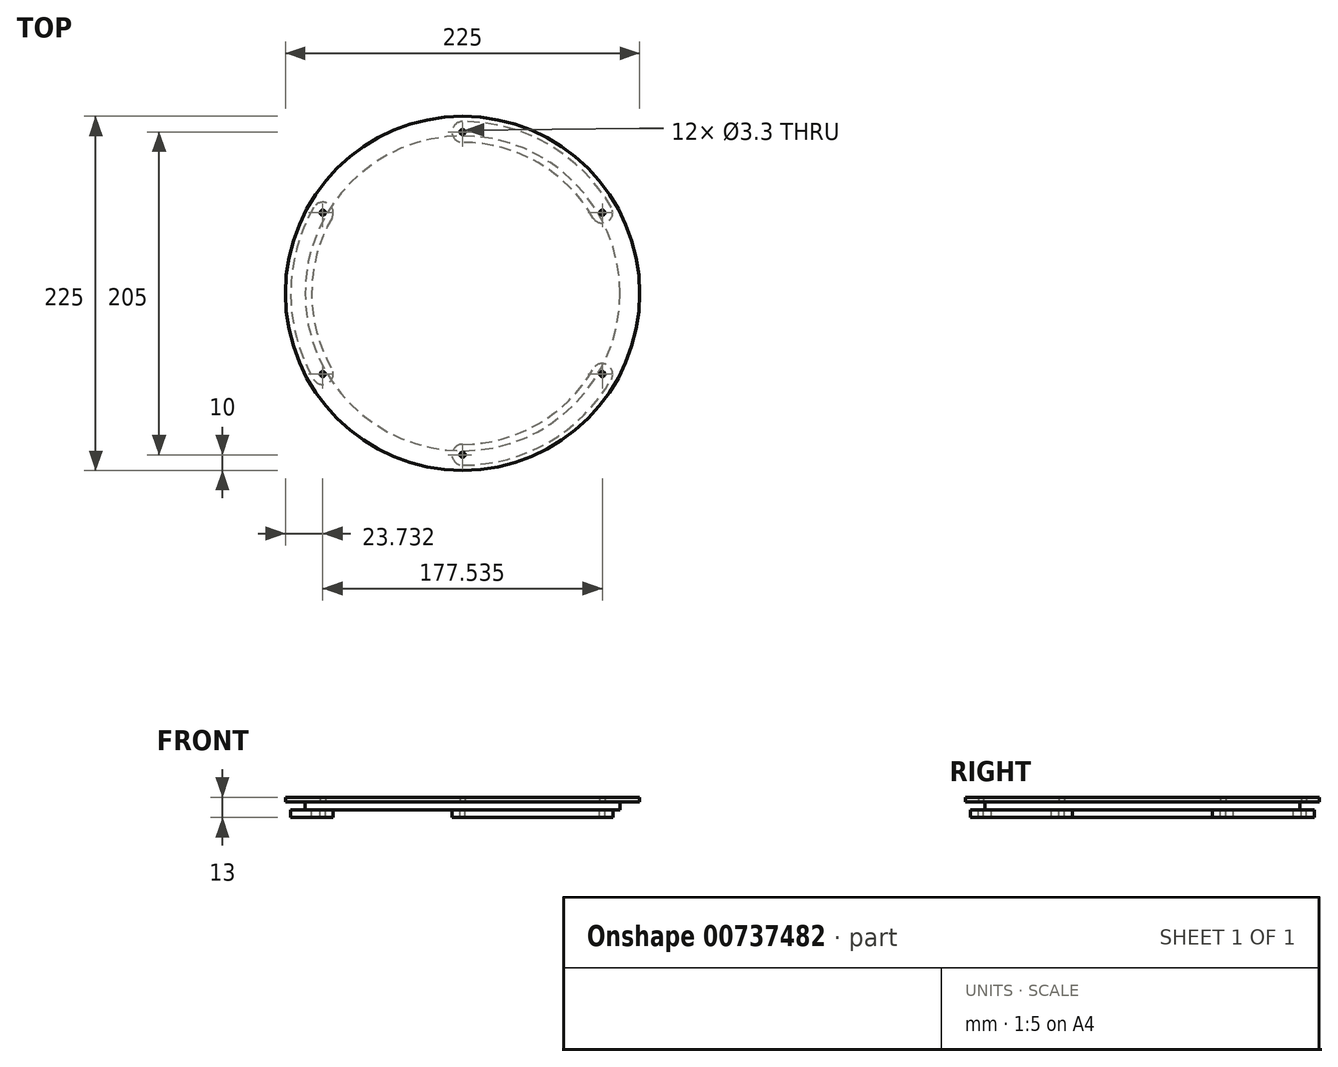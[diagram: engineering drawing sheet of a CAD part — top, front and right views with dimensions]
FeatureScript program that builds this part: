
annotation { "Feature Type Name" : "Feature", "Feature Type Description" : "" }
export const myFeature = defineFeature(function(context is Context, id is Id, definition is map)
    precondition{}
    {
        {
            var Q0;
            Q0=qCreatedBy(makeId("Top.planeOp"),FACE);
            var sketch = newSketch(context, id + "F0", { "sketchPlane" : qUnion([Q0])});
            skCircle(sketch, "E0", {"center": v(0, 0) * mm, "radius": 112.5 * mm});
            skPoint(sketch, "E1", {"position": v(0, 102.5) * mm});
            skPoint(sketch, "E2.1.0", {"position": v(-88.77, 51.25) * mm});
            skPoint(sketch, "E2.2.0", {"position": v(-88.77, -51.25) * mm});
            skPoint(sketch, "E2.3.0", {"position": v(0, -102.5) * mm});
            skPoint(sketch, "E2.4.0", {"position": v(88.77, -51.25) * mm});
            skPoint(sketch, "E2.5.0", {"position": v(88.77, 51.25) * mm});
            skSolve(sketch);
        }
        {
            var Q0;
            Q0=makeQuery(id+"F0.imprint","IMPRINT",FACE,{"disambiguationData":[TD([[makeQuery(id+"F0.imprint","IMPRINT",EDGE,{"derivedFrom":sQuery(id+"F0.wireOp",EDGE,"E0")}),1.0]])]});
            extrude(context, id + "F1", {"entities" : qUnion([Q0]), "depth" : 3 * mm, "offsetDistance" : 25 * mm});
        }
        {
            var Q0;
            Q0=sQuery(id+"F0.wireOp",VERTEX,"E1");
            var Q1;
            Q1=sQuery(id+"F0.wireOp",VERTEX,"E2.1.0");
            var Q2;
            Q2=sQuery(id+"F0.wireOp",VERTEX,"E2.2.0");
            var Q3;
            Q3=sQuery(id+"F0.wireOp",VERTEX,"E2.3.0");
            var Q4;
            Q4=sQuery(id+"F0.wireOp",VERTEX,"E2.4.0");
            var Q5;
            Q5=sQuery(id+"F0.wireOp",VERTEX,"E2.5.0");
            var Q6;
            Q6=makeQuery(id+"F1.opExtrude","SWEPT_BODY",BODY,{"disambiguationData":[OSD([sQuery(id+"F0.wireOp",EDGE,"E0")])]});
            hole(context, id + "F2", {"style" : HoleStyle.SIMPLE, "endStyle" : HoleEndStyle.BLIND, "oppositeDirection" : true, "standardTappedOrClearance" : lookupTablePath({ "standard" : "ISO", "fit" : "Normal", "size" : "M3", "type" : "Clearance" }), "standardBlindInLast" : lookupTablePath({ "fit" : "Standard", "standard" : "ISO", "size" : "M3", "type" : "Clearance" }), "holeDiameter" : 3.3 * mm, "majorDiameter" : 5 * mm, "holeDepth" : 15 * mm, "isTappedThrough" : true, "tappedDepth" : 8.5 * mm, "tapClearance" : 3, "startFromSketch" : true, "locations" : qUnion([Q0, Q1, Q2, Q3, Q4, Q5]), "scope" : qUnion([Q6])});
        }
        {
            var Q0;
            Q0=makeQuery(id+"F0.imprint","IMPRINT",FACE,{"disambiguationData":[TD([[makeQuery(id+"F0.imprint","IMPRINT",EDGE,{"derivedFrom":sQuery(id+"F0.wireOp",EDGE,"E0")}),1.0]])]});
            var sketch = newSketch(context, id + "F3", { "sketchPlane" : qUnion([Q0])});
            skCircle(sketch, "E3", {"center": v(0, 0) * mm, "radius": 100 * mm});
            skSolve(sketch);
        }
        {
            var Q0;
            Q0=makeQuery(id+"F3.imprint","IMPRINT",FACE,{"disambiguationData":[TD([[makeQuery(id+"F3.imprint","IMPRINT",EDGE,{"derivedFrom":sQuery(id+"F3.wireOp",EDGE,"E3")}),1.0]])]});
            extrude(context, id + "F4", {"entities" : qUnion([Q0]), "oppositeDirection" : true, "depth" : 5 * mm, "offsetDistance" : 25 * mm});
        }
        {
            var Q0;
            Q0=makeQuery(id+"F4.opExtrude","CAP_FACE",FACE,{"disambiguationData":[OSD([sQuery(id+"F3.wireOp",EDGE,"E3")])],"isStart":false});
            var sketch = newSketch(context, id + "F5", { "sketchPlane" : qUnion([Q0])});
            skCircle(sketch, "E4", {"center": v(0, -102.5) * mm, "radius": 6.65 * mm});
            skCircle(sketch, "E5", {"center": v(88.77, -51.25) * mm, "radius": 6.65 * mm});
            skArc(sketch, "E6", {"start": v(0, -109.15) * mm, "mid": v(54.57, -94.53) * mm, "end": v(94.53, -54.58) * mm});
            skArc(sketch, "E7", {"start": v(0, -95.85) * mm, "mid": v(47.92, -83) * mm, "end": v(83, -47.93) * mm});
            skCircle(sketch, "E8.0", {"center": v(0, -102.5) * mm, "radius": 1.65 * mm});
            skCircle(sketch, "E8.1", {"center": v(88.77, -51.25) * mm, "radius": 1.65 * mm});
            skSolve(sketch);
        }
        {
            var Q0;
            {var subQ0=sQuery(id+"F5.wireOp",EDGE,"E4");var subQ1=makeQuery(id+"F5.imprint","INTERSECT",VERTEX,{"derivedFrom":[subQ0,sQuery(id+"F5.wireOp",EDGE,"E7")]});Q0=makeQuery(id+"F5.imprint","IMPRINT",FACE,{"disambiguationData":[TD([[makeQuery(id+"F5.imprint","IMPRINT",EDGE,{"disambiguationData":[TD([[subQ1,1.0]])],"derivedFrom":subQ0}),1.0]])]});}
            var Q1;
            {var subQ0=sQuery(id+"F5.wireOp",EDGE,"E4");var subQ1=makeQuery(id+"F5.imprint","INTERSECT",VERTEX,{"derivedFrom":[subQ0,sQuery(id+"F5.wireOp",EDGE,"E6")]});Q1=makeQuery(id+"F5.imprint","IMPRINT",FACE,{"disambiguationData":[TD([[makeQuery(id+"F5.imprint","IMPRINT",EDGE,{"disambiguationData":[TD([[subQ1,1.0]])],"derivedFrom":subQ0}),1.0]])]});}
            var Q2;
            {var subQ0=sQuery(id+"F5.wireOp",EDGE,"E7");Q2=makeQuery(id+"F5.imprint","IMPRINT",FACE,{"disambiguationData":[TD([[makeQuery(id+"F5.imprint","IMPRINT",EDGE,{"derivedFrom":subQ0}),-1.0]])]});}
            var Q3;
            {var subQ0=sQuery(id+"F5.wireOp",EDGE,"E6");Q3=makeQuery(id+"F5.imprint","IMPRINT",FACE,{"disambiguationData":[TD([[makeQuery(id+"F5.imprint","IMPRINT",EDGE,{"derivedFrom":subQ0}),1.0]])]});}
            var Q4;
            {var subQ0=sQuery(id+"F5.wireOp",EDGE,"E5");var subQ1=makeQuery(id+"F5.imprint","INTERSECT",VERTEX,{"derivedFrom":[subQ0,sQuery(id+"F5.wireOp",EDGE,"E7")]});Q4=makeQuery(id+"F5.imprint","IMPRINT",FACE,{"disambiguationData":[TD([[makeQuery(id+"F5.imprint","IMPRINT",EDGE,{"disambiguationData":[TD([[subQ1,1.0]])],"derivedFrom":subQ0}),1.0]])]});}
            var Q5;
            {var subQ0=sQuery(id+"F5.wireOp",EDGE,"E5");var subQ1=makeQuery(id+"F5.imprint","INTERSECT",VERTEX,{"derivedFrom":[subQ0,sQuery(id+"F5.wireOp",EDGE,"E6")]});Q5=makeQuery(id+"F5.imprint","IMPRINT",FACE,{"disambiguationData":[TD([[makeQuery(id+"F5.imprint","IMPRINT",EDGE,{"disambiguationData":[TD([[subQ1,1.0]])],"derivedFrom":subQ0}),1.0]])]});}
            extrude(context, id + "F6", {"entities" : qUnion([Q0, Q1, Q2, Q3, Q4, Q5]), "depth" : 5 * mm, "offsetDistance" : 25 * mm});
        }
        {
            var Q0;
            Q0=qCreatedBy(makeId("Front.planeOp"),FACE);
            var sketch = newSketch(context, id + "F7", { "sketchPlane" : qUnion([Q0])});
            skLineSegment(sketch, "E9", {"start": v(0, 0) * mm, "end": v(0, -38.9) * mm, "construction": true});
            skSolve(sketch);
        }
        {
            var Q0;
            Q0=makeQuery(id+"F6.opExtrude","SWEPT_BODY",BODY,{"disambiguationData":[OSD([sQuery(id+"F5.wireOp",EDGE,"E4"),sQuery(id+"F5.wireOp",EDGE,"E5"),sQuery(id+"F5.wireOp",EDGE,"E6"),sQuery(id+"F5.wireOp",EDGE,"E7"),sQuery(id+"F5.wireOp",EDGE,"E8.0"),sQuery(id+"F5.wireOp",EDGE,"E8.1")])]});
            var Q1;
            Q1=sQuery(id+"F7.wireOp",EDGE,"E9");
            circularPattern(context, id + "F8", {"entities" : qUnion([Q0]), "axis" : qUnion([Q1]), "angle" : 360 * degree, "instanceCount" : 3, "equalSpace" : true});
        }
    });
